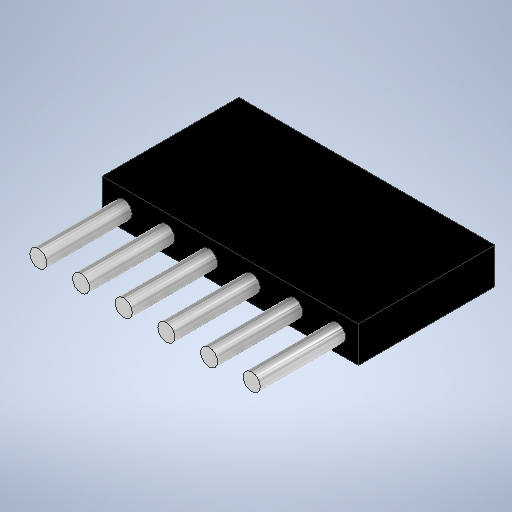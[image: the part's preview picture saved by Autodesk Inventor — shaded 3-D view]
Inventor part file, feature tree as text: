
AUTODESK INVENTOR PART (.ipt)
format: ipt  version: 2025.2 (Build 292293000, 293)  size: 278,016 bytes
history: native  units: mm
features: extrude x2, sketch x2
ambient origin geometry x8: Origin, YZ Plane, XZ Plane, XY Plane, X Axis, Y Axis, Z Axis, Center Point
bodies: Solid1 (feature_tree)
feature tree (4):
  extrude  "Extrusion1"  Depth=8.0mm
  extrude  "Extrusion2"  Depth=5.0mm
  sketch  "Sketch1"  dims[d0=15.0mm d1=8.0mm]
  sketch  "Sketch2"  dims[d2=2.1mm d3=0.0mm d4=1.0mm d5=1.0mm d6=1.0mm d7=1.0mm d8=1.0mm d9=1.0mm d10=1.05mm d11=1.05mm d12=1.05mm d13=1.05mm d14=1.05mm d15=1.05mm d16=1.25mm d17=2.5mm d18=2.5mm d19=1.25mm d20=2.5mm d21=2.5mm d22=5.0mm d23=0.0mm]
